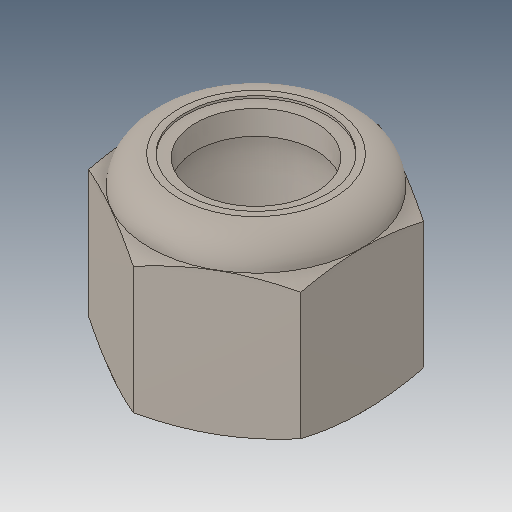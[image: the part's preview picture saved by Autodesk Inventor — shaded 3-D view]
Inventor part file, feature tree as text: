
AUTODESK INVENTOR PART (.ipt)
format: ipt  version: 2023.5 (Build 275446000, 446)  size: 176,128 bytes
history: native  units: in
note: dims shown in document units (in); Inventor stores cm internally (conversion verified against a paired STEP export)
features: other x1, revolve x1
ambient origin geometry x8: Origin, YZ Plane, XZ Plane, XY Plane, X Axis, Y Axis, Z Axis, Center Point
bodies: Solid1 (feature_tree), Solid2 (feature_tree)
feature tree (2):
  other  "Cut-Revolve2"
  revolve  "Revolve1"  [1 undecoded]
note: 1 required parameter value undecoded (feature->parameter linkage not recoverable at this tier; creation-order binding heuristic only, values carry confidence <= 0.55)
